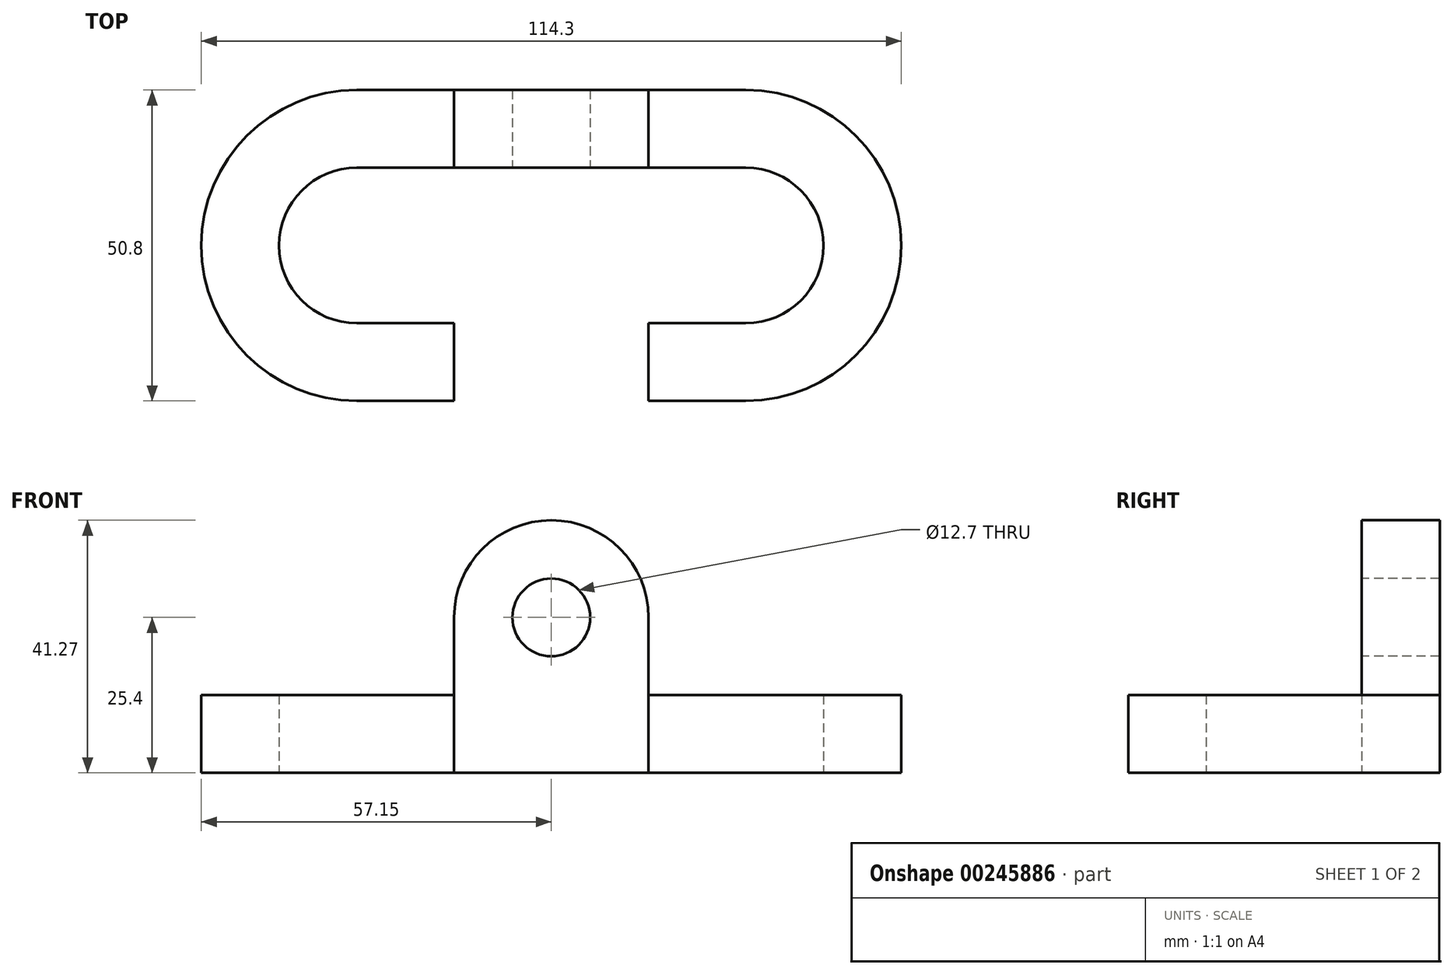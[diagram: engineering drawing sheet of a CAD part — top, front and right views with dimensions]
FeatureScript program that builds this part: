
annotation { "Feature Type Name" : "Feature", "Feature Type Description" : "" }
export const myFeature = defineFeature(function(context is Context, id is Id, definition is map)
    precondition{}
    {
        {
            var Q0;
            Q0=qCreatedBy(makeId("Top.planeOp"),FACE);
            var sketch = newSketch(context, id + "F0", { "sketchPlane" : qUnion([Q0])});
            skArc(sketch, "E0", {"start": v(31.75, -25.4) * mm, "mid": v(57.15, 0) * mm, "end": v(31.75, 25.4) * mm});
            skArc(sketch, "E1", {"start": v(31.75, -12.7) * mm, "mid": v(44.45, 0) * mm, "end": v(31.75, 12.7) * mm});
            skLineSegment(sketch, "E2", {"start": v(31.75, 25.4) * mm, "end": v(31.75, 37.32) * mm, "construction": true});
            skLineSegment(sketch, "E3", {"start": v(31.75, 25.4) * mm, "end": v(-4.95, 25.4) * mm});
            skLineSegment(sketch, "E4", {"start": v(31.75, 12.7) * mm, "end": v(-12.27, 12.7) * mm});
            skLineSegment(sketch, "E5.MirrorCS", {"start": v(-31.75, 12.7) * mm, "end": v(12.27, 12.7) * mm});
            skLineSegment(sketch, "E6.MirrorCS", {"start": v(-31.75, 25.4) * mm, "end": v(4.95, 25.4) * mm});
            skArc(sketch, "E7.MirrorCS", {"start": v(-31.75, -25.4) * mm, "mid": v(-57.15, 0) * mm, "end": v(-31.75, 25.4) * mm});
            skArc(sketch, "E8.MirrorCS", {"start": v(-31.75, -12.7) * mm, "mid": v(-44.45, 0) * mm, "end": v(-31.75, 12.7) * mm});
            skLineSegment(sketch, "E9", {"start": v(31.75, -12.7) * mm, "end": v(15.88, -12.7) * mm});
            skLineSegment(sketch, "E10", {"start": v(15.88, -12.7) * mm, "end": v(15.88, -25.4) * mm});
            skLineSegment(sketch, "E11", {"start": v(15.88, -25.4) * mm, "end": v(31.75, -25.4) * mm});
            skLineSegment(sketch, "E12.MirrorCS", {"start": v(-31.75, -12.7) * mm, "end": v(-15.88, -12.7) * mm});
            skLineSegment(sketch, "E13.MirrorCS", {"start": v(-15.88, -12.7) * mm, "end": v(-15.88, -25.4) * mm});
            skLineSegment(sketch, "E14.MirrorCS", {"start": v(-15.88, -25.4) * mm, "end": v(-31.75, -25.4) * mm});
            skPoint(sketch, "E15.MirrorCS.end.orphan", {"position": v(-31.75, -25.4) * mm});
            skPoint(sketch, "E15.MirrorCS.start.orphan", {"position": v(-31.75, -12.7) * mm});
            skSolve(sketch);
        }
        {
            var Q0;
            Q0=makeQuery(id+"F0.imprint","IMPRINT",FACE,{"disambiguationData":[TD([[makeQuery(id+"F0.imprint","IMPRINT",EDGE,{"derivedFrom":sQuery(id+"F0.wireOp",EDGE,"E0")}),1.0]])]});
            extrude(context, id + "F1", {"entities" : qUnion([Q0]), "depth" : 12.7 * mm});
        }
        {
            var Q0;
            Q0=makeQuery(id+"F1.opExtrude","SWEPT_FACE",FACE,{"disambiguationData":[OSD([sQuery(id+"F0.wireOp",EDGE,"E4"),sQuery(id+"F0.wireOp",EDGE,"E5.MirrorCS")])]});
            var sketch = newSketch(context, id + "F2", { "sketchPlane" : qUnion([Q0])});
            skArc(sketch, "E16", {"start": v(15.88, 25.4) * mm, "mid": v(0, 41.28) * mm, "end": v(-15.88, 25.4) * mm});
            skCircle(sketch, "E17", {"center": v(0, 25.4) * mm, "radius": 6.35 * mm});
            skLineSegment(sketch, "E18", {"start": v(15.88, 25.4) * mm, "end": v(15.88, 10.95) * mm, "construction": true});
            skLineSegment(sketch, "E19", {"start": v(-15.88, 25.4) * mm, "end": v(-15.88, 10.95) * mm, "construction": true});
            skLineSegment(sketch, "E20", {"start": v(-15.88, 25.4) * mm, "end": v(-15.88, 10.95) * mm});
            skLineSegment(sketch, "E21", {"start": v(15.88, 25.4) * mm, "end": v(15.88, 10.95) * mm});
            skLineSegment(sketch, "E22", {"start": v(-15.88, 10.95) * mm, "end": v(15.88, 10.95) * mm});
            skSolve(sketch);
        }
        {
            var Q0;
            Q0=makeQuery(id+"F2.imprint","IMPRINT",FACE,{"disambiguationData":[TD([[makeQuery(id+"F2.imprint","IMPRINT",EDGE,{"derivedFrom":sQuery(id+"F2.wireOp",EDGE,"E16")}),1.0]])]});
            extrude(context, id + "F3", {"entities" : qUnion([Q0]), "operationType" : NewBodyOperationType.ADD, "oppositeDirection" : true, "depth" : 12.7 * mm});
        }
    });
